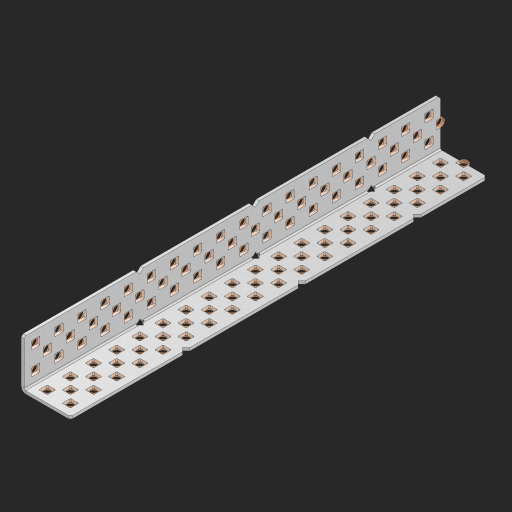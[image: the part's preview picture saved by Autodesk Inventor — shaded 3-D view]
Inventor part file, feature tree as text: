
AUTODESK INVENTOR PART (.ipt)
format: ipt  version: 2023 (Build 270158000, 158)  size: 1,433,600 bytes
history: native  units: in
note: dims shown in document units (in); Inventor stores cm internally (conversion verified against a paired STEP export)
features: other x114, extrude x106, sheet_metal_op x8, sketch x7, pattern_linear x2, mirror x1, chamfer x1
ambient origin geometry x8: Origin, YZ Plane, XZ Plane, XY Plane, X Axis, Y Axis, Z Axis, Center Point
bodies: Solid1 (feature_tree), Body (feature_tree)
feature tree (239):
  sheet_metal_op  "Flanges"
  sheet_metal_op  "Body Pattern"
  pattern_linear  "Center Pattern"  Spacing1=1.0in  [1 undecoded]
  other  "Arc Length"
  pattern_linear  "Notch Pattern"  Spacing1=0.25in  [1 undecoded]
  other  "Diagonal Plane"
  mirror  "Everything Mirrored"
  chamfer  "End Chamfer"
  sketch  "Sketch1"  dims[d0=1.0in]
  other  "Plate1"
  sketch  "Sketch2"  dims[d1=9.0in]
  other  "Plate2"
  sheet_metal_op  "Bend1"
  sheet_metal_op  "Corner1"
  sketch  "Sketch8"  dims[d2=0.0625in]
  sketch  "Sketch9"  dims[d3=0.0625in]
  other  "Srf91"
  sheet_metal_op  "Body Pattern Sketch"
  other  "Srf92"
  sketch  "Sketch13"  dims[d4=0.0312in]
  sketch  "Sketch15"  dims[d5=0.125in]
  sketch  "Sketch16"  dims[d6=0.0625in d7=1.0in d8=90.0deg d9=0.0312in d10=0.25in d11=0.0625in d12=0.0625in d49=0.182in d50=0.02in d52=0.25in d53=0.0625in d54=0.0in d55=0.172in d56=1.0in d57=0.0in d60=7.0866in d62=0.5in d63=0.7874in d65=0.5in d85=0.1473in d86=0.1782in d89=0.0625in d90=0.0in d91=0.04in d92=0.0491in d95=2.5in d96=0.04in d97=0.25in d98=45.0deg d99=0.25in d106=0.182in d107=0.02in d108=0.5in d110=0.0625in d111=0.0in d112=0.172in d113=0.5in d114=0.0in d117=0.5in d123=0.25in d125=0.25in d126=0.0491in d127=0.1473in d128=0.08in d129=0.04in d130=2.5in]
  other  "Srf786"
  other  "Srf856"
  other  "Srf857"
  other  "Srf858"
  other  "Srf859"
  other  "Srf860"
  other  "Srf861"
  other  "Srf889"
  other  "Srf890"
  other  "Srf891"
  other  "Srf1275"
  other  "Srf1276"
  other  "Srf1278"
  other  "Srf1279"
  other  "Srf1280"
  other  "Srf1281"
  other  "Srf1282"
  other  "Srf1283"
  other  "Srf1277"
  other  "Srf1285"
  other  "Srf1286"
  other  "Srf1287"
  other  "Srf1383"
  other  "Srf1384"
  other  "Srf1385"
  other  "Srf1386"
  other  "Srf1387"
  other  "Srf1388"
  other  "Srf1389"
  other  "Srf1390"
  other  "Srf1391"
  other  "Srf1392"
  other  "Srf1393"
  other  "Srf1394"
  other  "Srf1395"
  other  "Srf1396"
  other  "Srf1397"
  other  "Srf1398"
  other  "Srf1399"
  other  "Srf1400"
  other  "Srf1401"
  other  "Srf1402"
  other  "Srf1403"
  other  "Srf1404"
  other  "Srf1405"
  other  "Srf1406"
  other  "Srf1407"
  other  "Srf1408"
  other  "Srf1409"
  other  "Srf1410"
  other  "Srf1445"
  other  "Srf1446"
  other  "Srf1447"
  other  "Srf1448"
  other  "Srf1449"
  other  "Srf1450"
  other  "Srf1451"
  other  "Srf1452"
  other  "Srf1453"
  other  "Srf1454"
  other  "Srf1455"
  other  "Srf1456"
  other  "Srf1457"
  other  "Srf1458"
  other  "Srf1475"
  other  "Srf1476"
  other  "Srf1477"
  other  "Srf1478"
  other  "Srf1479"
  other  "Srf1480"
  other  "Srf1481"
  other  "Srf1482"
  other  "Srf1483"
  other  "Srf1484"
  other  "Srf1485"
  other  "Srf1486"
  other  "Srf1487"
  other  "Srf1488"
  other  "Srf1489"
  other  "Srf1490"
  other  "Srf1491"
  other  "Srf1492"
  other  "Srf1493"
  other  "Srf1494"
  other  "Srf1495"
  other  "Srf1496"
  other  "Srf1497"
  other  "Srf1498"
  other  "Srf1499"
  other  "Srf1500"
  other  "Srf1501"
  other  "Srf1502"
  other  "Srf1537"
  other  "Srf1538"
  other  "Srf1539"
  other  "Srf1540"
  other  "Srf1541"
  other  "Srf1542"
  other  "Srf1543"
  other  "Srf1544"
  other  "Srf1545"
  other  "Srf1546"
  other  "Srf1547"
  other  "Srf1548"
  other  "Srf1549"
  other  "Srf1550"
  sheet_metal_op  "Body Stamp"
  sheet_metal_op  "Body Circle"
  other  "Center Stamp"
  other  "Center Circle"
  sheet_metal_op  "Notch"
  extrude  "ExtrusionSrf92"  Depth=0.0625in
  extrude  "ExtrusionSrf856"  Depth=0.0625in
  extrude  "ExtrusionSrf857"  Depth=0.182in
  extrude  "ExtrusionSrf858"  Depth=0.02in
  extrude  "ExtrusionSrf859"  Depth=0.25in
  extrude  "ExtrusionSrf860"  Depth=0.0625in
  extrude  "ExtrusionSrf861"  TaperAngle=0.0deg  [1 undecoded]
  extrude  "ExtrusionSrf889"  Depth=2.5in
  extrude  "ExtrusionSrf890"  Depth=1.0in TaperAngle=0.0deg
  extrude  "ExtrusionSrf891"  Depth=2.5in
  extrude  "ExtrusionSrf1275"  Depth=0.5in
  extrude  "ExtrusionSrf1276"  Depth=2.5in
  extrude  "ExtrusionSrf1277"  Depth=2.5in
  extrude  "ExtrusionSrf1278"  Depth=0.0625in
  extrude  "ExtrusionSrf1279"  Depth=2.5in TaperAngle=0.0deg
  extrude  "ExtrusionSrf1280"  Depth=2.5in
  extrude  "ExtrusionSrf1281"  Depth=0.25in TaperAngle=45.0deg
  extrude  "ExtrusionSrf1282"  Depth=0.25in
  extrude  "ExtrusionSrf1345"  Depth=0.182in
  extrude  "ExtrusionSrf1346"  Depth=0.02in
  extrude  "ExtrusionSrf1347"  Depth=0.5in
  extrude  "ExtrusionSrf1348"  Depth=0.0625in
  extrude  "ExtrusionSrf1383"  TaperAngle=0.0deg  [1 undecoded]
  extrude  "ExtrusionSrf1384"  Depth=2.5in
  extrude  "ExtrusionSrf1385"  Depth=0.5in TaperAngle=0.0deg
  extrude  "ExtrusionSrf1386"  Depth=0.5in
  extrude  "ExtrusionSrf1387"  Depth=0.25in
  extrude  "ExtrusionSrf1388"  Depth=0.25in
  extrude  "ExtrusionSrf1389"  Depth=2.5in
  extrude  "ExtrusionSrf1390"  Depth=2.5in
  extrude  "ExtrusionSrf1391"  Depth=2.5in
  extrude  "ExtrusionSrf1392"  Depth=2.5in
  extrude  "ExtrusionSrf1393"  Depth=2.5in
  extrude  "ExtrusionSrf1394"  [1 undecoded]
  extrude  "ExtrusionSrf1395"  [1 undecoded]
  extrude  "ExtrusionSrf1396"  [1 undecoded]
  extrude  "ExtrusionSrf1397"  [1 undecoded]
  extrude  "ExtrusionSrf1398"  [1 undecoded]
  extrude  "ExtrusionSrf1399"  [1 undecoded]
  extrude  "ExtrusionSrf1400"  [1 undecoded]
  extrude  "ExtrusionSrf1401"  [1 undecoded]
  extrude  "ExtrusionSrf1402"  [1 undecoded]
  extrude  "ExtrusionSrf1403"  [1 undecoded]
  extrude  "ExtrusionSrf1404"  [1 undecoded]
  extrude  "ExtrusionSrf1405"  [1 undecoded]
  extrude  "ExtrusionSrf1406"  [1 undecoded]
  extrude  "ExtrusionSrf1407"  [1 undecoded]
  extrude  "ExtrusionSrf1408"  [1 undecoded]
  extrude  "ExtrusionSrf1409"  [1 undecoded]
  extrude  "ExtrusionSrf1410"  [1 undecoded]
  extrude  "ExtrusionSrf1445"  [1 undecoded]
  extrude  "ExtrusionSrf1446"  [1 undecoded]
  extrude  "ExtrusionSrf1447"  [1 undecoded]
  extrude  "ExtrusionSrf1448"  [1 undecoded]
  extrude  "ExtrusionSrf1449"  [1 undecoded]
  extrude  "ExtrusionSrf1450"  [1 undecoded]
  extrude  "ExtrusionSrf1451"  [1 undecoded]
  extrude  "ExtrusionSrf1452"  [1 undecoded]
  extrude  "ExtrusionSrf1453"  [1 undecoded]
  extrude  "ExtrusionSrf1454"  [1 undecoded]
  extrude  "ExtrusionSrf1455"  [1 undecoded]
  extrude  "ExtrusionSrf1456"  [1 undecoded]
  extrude  "ExtrusionSrf1457"  [1 undecoded]
  extrude  "ExtrusionSrf1458"  [1 undecoded]
  extrude  "ExtrusionSrf1475"  [1 undecoded]
  extrude  "ExtrusionSrf1476"  [1 undecoded]
  extrude  "ExtrusionSrf1477"  [1 undecoded]
  extrude  "ExtrusionSrf1478"  [1 undecoded]
  extrude  "ExtrusionSrf1479"  [1 undecoded]
  extrude  "ExtrusionSrf1480"  [1 undecoded]
  extrude  "ExtrusionSrf1481"  [1 undecoded]
  extrude  "ExtrusionSrf1482"  [1 undecoded]
  extrude  "ExtrusionSrf1483"  [1 undecoded]
  extrude  "ExtrusionSrf1484"  [1 undecoded]
  extrude  "ExtrusionSrf1485"  [1 undecoded]
  extrude  "ExtrusionSrf1486"  [1 undecoded]
  extrude  "ExtrusionSrf1487"  [1 undecoded]
  extrude  "ExtrusionSrf1488"  [1 undecoded]
  extrude  "ExtrusionSrf1489"  [1 undecoded]
  extrude  "ExtrusionSrf1490"  [1 undecoded]
  extrude  "ExtrusionSrf1491"  [1 undecoded]
  extrude  "ExtrusionSrf1492"  [1 undecoded]
  extrude  "ExtrusionSrf1493"  [1 undecoded]
  extrude  "ExtrusionSrf1494"  [1 undecoded]
  extrude  "ExtrusionSrf1495"  [1 undecoded]
  extrude  "ExtrusionSrf1496"  [1 undecoded]
  extrude  "ExtrusionSrf1497"  [1 undecoded]
  extrude  "ExtrusionSrf1498"  [1 undecoded]
  extrude  "ExtrusionSrf1499"  [1 undecoded]
  extrude  "ExtrusionSrf1500"  [1 undecoded]
  extrude  "ExtrusionSrf1501"  [1 undecoded]
  extrude  "ExtrusionSrf1502"  [1 undecoded]
  extrude  "ExtrusionSrf1537"  [1 undecoded]
  extrude  "ExtrusionSrf1538"  [1 undecoded]
  extrude  "ExtrusionSrf1539"  [1 undecoded]
  extrude  "ExtrusionSrf1540"  [1 undecoded]
  extrude  "ExtrusionSrf1541"  [1 undecoded]
  extrude  "ExtrusionSrf1542"  [1 undecoded]
  extrude  "ExtrusionSrf1543"  [1 undecoded]
  extrude  "ExtrusionSrf1544"  [1 undecoded]
  extrude  "ExtrusionSrf1545"  [1 undecoded]
  extrude  "ExtrusionSrf1546"  [1 undecoded]
  extrude  "ExtrusionSrf1547"  [1 undecoded]
  extrude  "ExtrusionSrf1548"  [1 undecoded]
  extrude  "ExtrusionSrf1549"  [1 undecoded]
  extrude  "ExtrusionSrf1550"  [1 undecoded]
note: 77 required parameter values undecoded (feature->parameter linkage not recoverable at this tier; creation-order binding heuristic only, values carry confidence <= 0.55)
